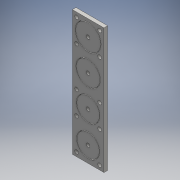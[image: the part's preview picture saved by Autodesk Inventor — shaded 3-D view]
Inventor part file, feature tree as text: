
AUTODESK INVENTOR PART (.ipt)
format: ipt  version: 2016 (Build 200138000, 138)  size: 195,584 bytes
history: native  units: mm
features: extrude x1, sketch x1
ambient origin geometry x8: Origin, YZ Plane, XZ Plane, XY Plane, X Axis, Y Axis, Z Axis, Center Point
bodies: Body1 (feature_tree)
feature tree (2):
  extrude  "Extrusion3"  Depth=6.39mm
  sketch  "Sketch1"  dims[d1=42.8241mm d2=33.8085mm d4=6.35mm d11=44.8241mm d12=6.35mm d13=6.35mm d14=6.35mm d15=54.0936mm d16=54.0936mm d17=54.0936mm d18=40.5702mm d19=42.5702mm d20=39.21786mm d21=41.21786mm d22=38.3163mm d23=40.3163mm d31=27.41205mm d32=27.41205mm d33=27.41205mm d34=27.41205mm d37=6.35mm d38=7.5mm d39=7.5mm d40=6.35mm d41=7.5mm d50=6.35mm d51=7.5mm d52=6.39mm d53=0.0mm]
